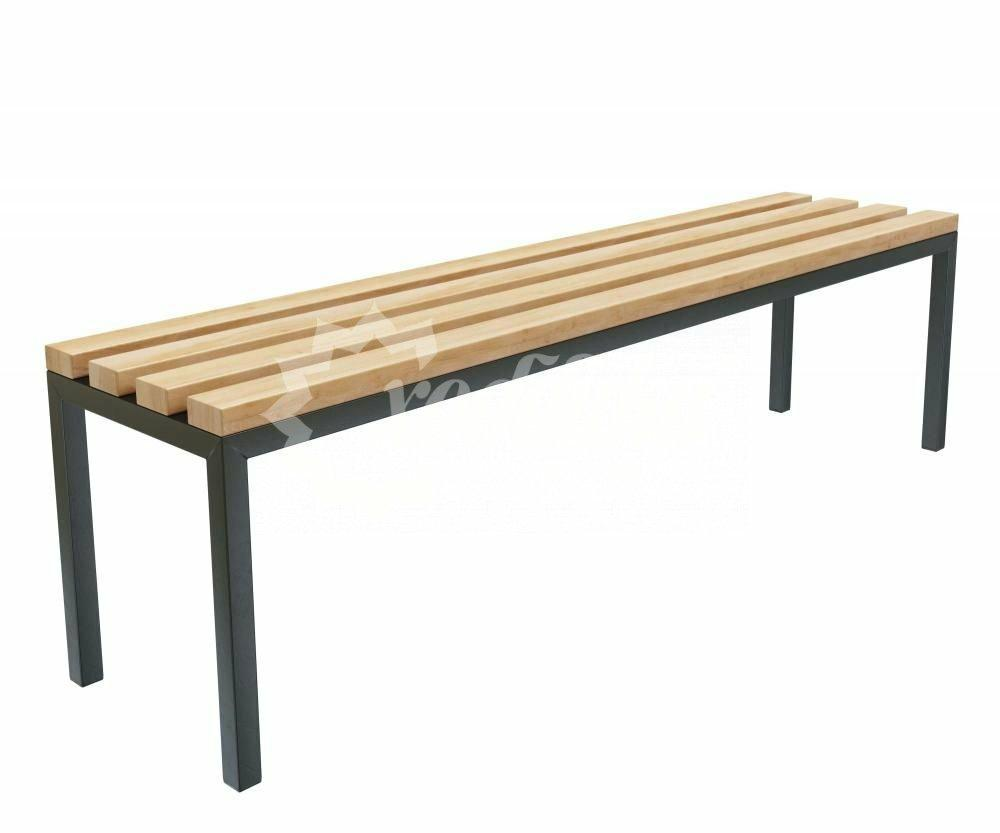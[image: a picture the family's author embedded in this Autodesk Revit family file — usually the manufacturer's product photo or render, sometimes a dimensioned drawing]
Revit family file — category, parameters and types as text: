
# Revit family: Банкетка для раздевалок «Бэйсик» Арт 20699
name_source: partatom
category: Антураж
revit_build: Autodesk Revit 2018 (Build: 20180423_1000(x64)
units: mm (PartAtom-declared; Revit-internal decimal feet)

## family parameters
Всегда вертикально = Да
Источник визуального образа = Геометрия семейства
На основе рабочей плоскости = Нет
Общий = Нет
При загрузке вырезать с полостями = Нет
Точка расчета площади = Нет

## types (2) — shared parameters
URL = https://hobbyka.ru
Артикул товара = Арт. 20699
Высота = 420 мм
Группа модели = Скамейки для раздевалок
Изготовитель = ООО «Хоббика»
Изображение типоразмера = Банкетка для раздевалок «Бэйсик» Арт 20699.jpg
Материал изделия = Сталь, дерево
Цвет лавки = Дерево
Цвет опор = Сталь
Ширина = 350 мм

## per-type parameters (varying)
| type | Версия 1,2 м | Версия 1,5 м | Длина | Описание |
| Версия 1,2 м | Да | Нет | 1200 мм | Банкетка для раздевалок «Бэйсик». Версия 1,2 м |
| Версия 1,5 м | Нет | Да | 1500 мм | Банкетка для раздевалок «Бэйсик». Версия 1,5 м |
